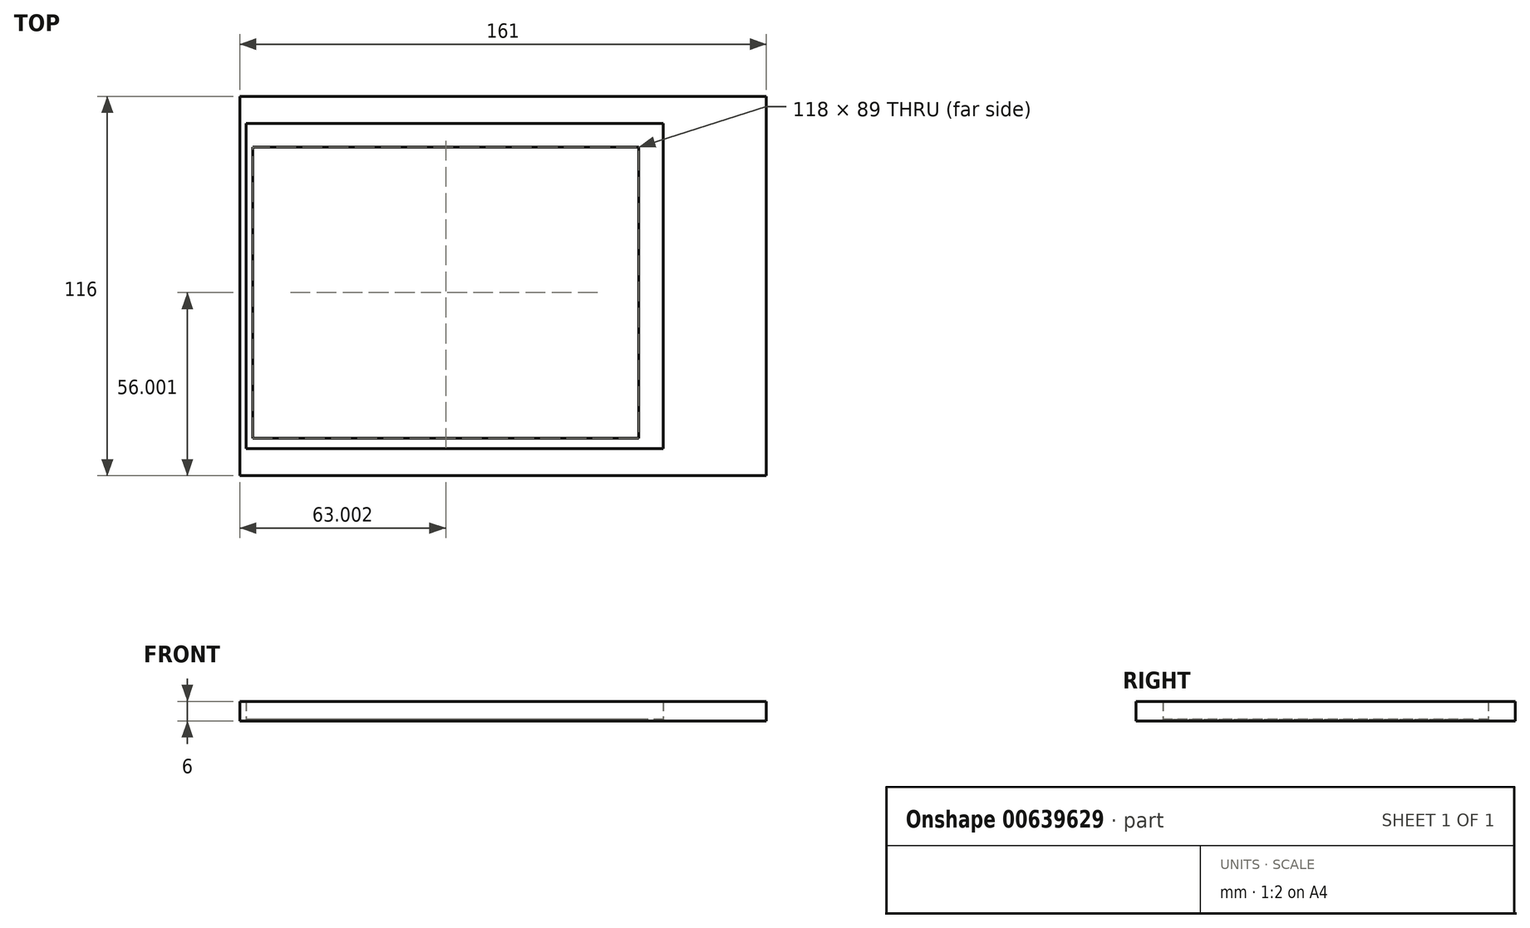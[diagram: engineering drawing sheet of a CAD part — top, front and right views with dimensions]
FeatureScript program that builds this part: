
annotation { "Feature Type Name" : "Feature", "Feature Type Description" : "" }
export const myFeature = defineFeature(function(context is Context, id is Id, definition is map)
    precondition{}
    {
        {
            var Q0;
            Q0=qCreatedBy(makeId("Top.planeOp"),FACE);
            var sketch = newSketch(context, id + "F0", { "sketchPlane" : qUnion([Q0])});
            skLineSegment(sketch, "E0.bottom", {"start": v(49.33, -50.84) * mm, "end": v(-68.67, -50.84) * mm});
            skLineSegment(sketch, "E0.top", {"start": v(49.33, 38.16) * mm, "end": v(-68.67, 38.16) * mm});
            skLineSegment(sketch, "E0.left", {"start": v(49.33, -50.84) * mm, "end": v(49.33, 38.16) * mm});
            skLineSegment(sketch, "E0.right", {"start": v(-68.67, -50.84) * mm, "end": v(-68.67, 38.16) * mm});
            skPoint(sketch, "E0.middle", {"position": v(-8.67, -6.34) * mm});
            skLineSegment(sketch, "E1", {"start": v(56.83, 45.41) * mm, "end": v(-70.67, 45.41) * mm});
            skLineSegment(sketch, "E2", {"start": v(-70.67, 45.41) * mm, "end": v(-70.67, -54.09) * mm});
            skLineSegment(sketch, "E3", {"start": v(-70.67, -54.09) * mm, "end": v(56.83, -54.09) * mm});
            skLineSegment(sketch, "E4", {"start": v(88.33, 53.66) * mm, "end": v(88.33, -62.34) * mm});
            skLineSegment(sketch, "E5", {"start": v(56.83, 45.41) * mm, "end": v(56.83, -54.09) * mm});
            skLineSegment(sketch, "E6", {"start": v(88.33, 53.66) * mm, "end": v(-72.67, 53.66) * mm});
            skLineSegment(sketch, "E7", {"start": v(-72.67, 53.66) * mm, "end": v(-72.67, -62.34) * mm});
            skLineSegment(sketch, "E8", {"start": v(-72.67, -62.34) * mm, "end": v(88.33, -62.34) * mm});
            skLineSegment(sketch, "E9", {"start": v(-122.06, -6.34) * mm, "end": v(95.64, -6.34) * mm, "construction": true});
            skLineSegment(sketch, "E10", {"start": v(-8.67, 69.3) * mm, "end": v(-8.67, -72.63) * mm, "construction": true});
            skSolve(sketch);
        }
        {
            var Q0;
            Q0=makeQuery(id+"F0.imprint","IMPRINT",FACE,{"disambiguationData":[TD([[makeQuery(id+"F0.imprint","IMPRINT",EDGE,{"derivedFrom":sQuery(id+"F0.wireOp",EDGE,"E0.bottom")}),1.0]])]});
            extrude(context, id + "F1", {"entities" : qUnion([Q0]), "depth" : 0.5 * mm, "offsetDistance" : 25 * mm});
        }
        {
            var Q0;
            Q0=makeQuery(id+"F0.imprint","IMPRINT",FACE,{"disambiguationData":[TD([[makeQuery(id+"F0.imprint","IMPRINT",EDGE,{"derivedFrom":sQuery(id+"F0.wireOp",EDGE,"E1")}),-1.0]])]});
            extrude(context, id + "F2", {"entities" : qUnion([Q0]), "operationType" : NewBodyOperationType.ADD, "depth" : 6 * mm, "offsetDistance" : 25 * mm});
        }
    });
